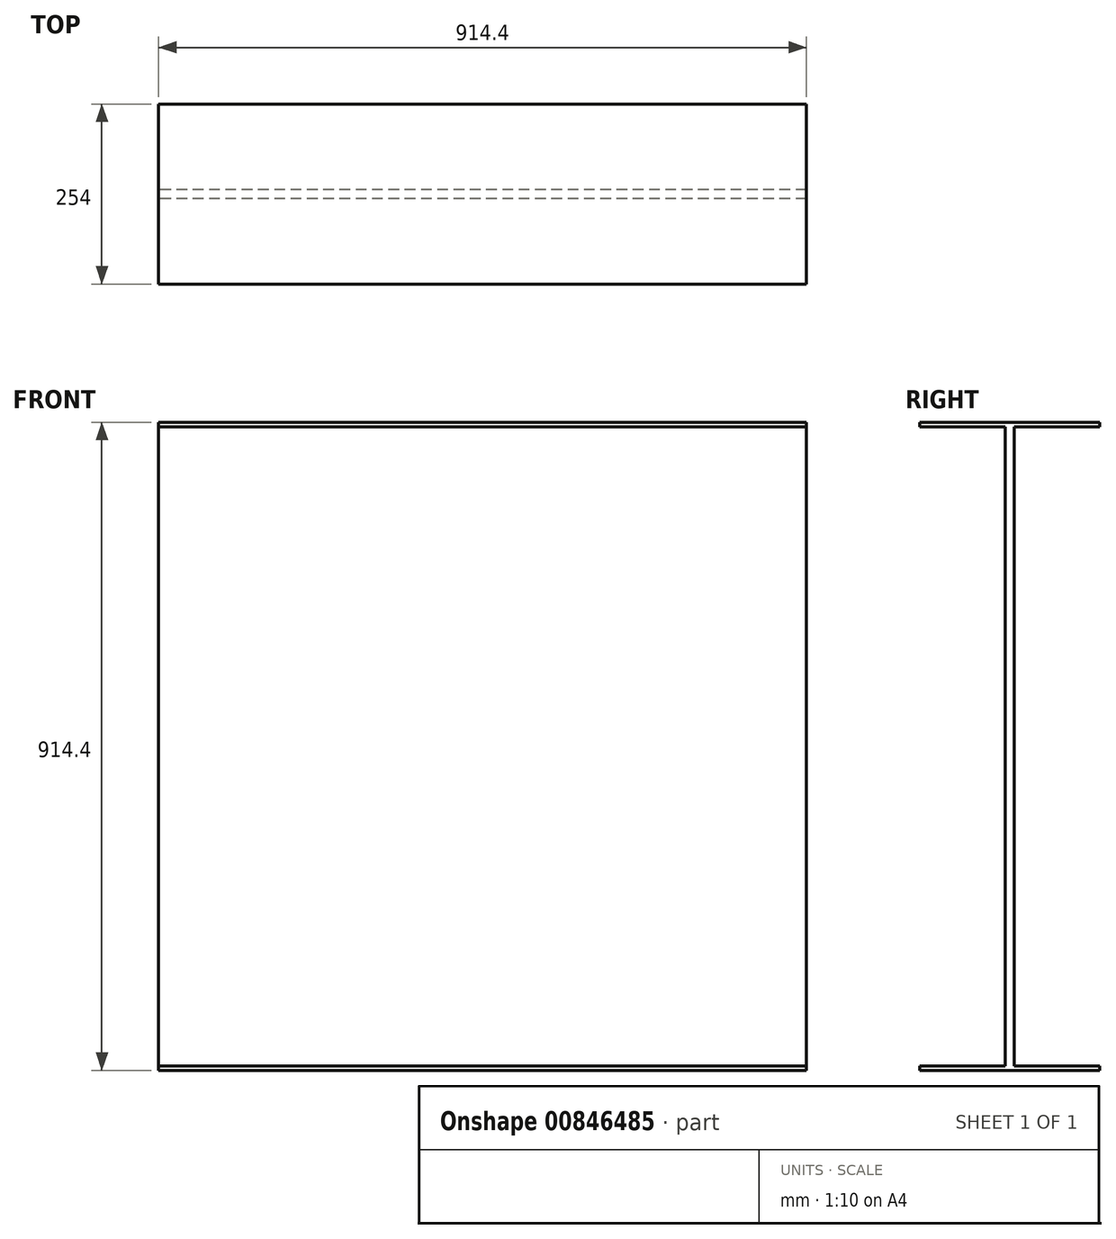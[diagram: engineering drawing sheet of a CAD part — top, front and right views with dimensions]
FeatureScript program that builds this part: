
annotation { "Feature Type Name" : "Feature", "Feature Type Description" : "" }
export const myFeature = defineFeature(function(context is Context, id is Id, definition is map)
    precondition{}
    {
        {
            var Q0;
            Q0=qCreatedBy(makeId("Right.planeOp"),FACE);
            var sketch = newSketch(context, id + "F0", { "sketchPlane" : qUnion([Q0])});
            skLineSegment(sketch, "E0", {"start": v(-127, 457.2) * mm, "end": v(127, 457.2) * mm});
            skLineSegment(sketch, "E1", {"start": v(127, 457.2) * mm, "end": v(127, 450.85) * mm});
            skLineSegment(sketch, "E2", {"start": v(127, 450.85) * mm, "end": v(6.35, 450.85) * mm});
            skLineSegment(sketch, "E3", {"start": v(6.35, 450.85) * mm, "end": v(6.35, -450.85) * mm});
            skLineSegment(sketch, "E4", {"start": v(6.35, -450.85) * mm, "end": v(127, -450.85) * mm});
            skLineSegment(sketch, "E5", {"start": v(-127, 457.2) * mm, "end": v(-127, 450.85) * mm});
            skLineSegment(sketch, "E6", {"start": v(-127, 450.85) * mm, "end": v(-6.35, 450.85) * mm});
            skLineSegment(sketch, "E7", {"start": v(-6.35, 450.85) * mm, "end": v(-6.35, -450.85) * mm});
            skLineSegment(sketch, "E8", {"start": v(-6.35, -450.85) * mm, "end": v(-127, -450.85) * mm});
            skLineSegment(sketch, "E9", {"start": v(-127, -450.85) * mm, "end": v(-127, -457.2) * mm});
            skLineSegment(sketch, "E10", {"start": v(-127, -457.2) * mm, "end": v(127, -457.2) * mm});
            skLineSegment(sketch, "E11", {"start": v(127, -457.2) * mm, "end": v(127, -450.85) * mm});
            skLineSegment(sketch, "E12", {"start": v(6.35, 450.85) * mm, "end": v(-6.35, -450.85) * mm, "construction": true});
            skSolve(sketch);
        }
        {
            var Q0;
            Q0 = qSketchRegion(id + "F0", true);
            extrude(context, id + "F1", {"entities" : qUnion([Q0]), "depth" : 914.4 * mm, "offsetDistance" : 25.4 * mm});
        }
    });
